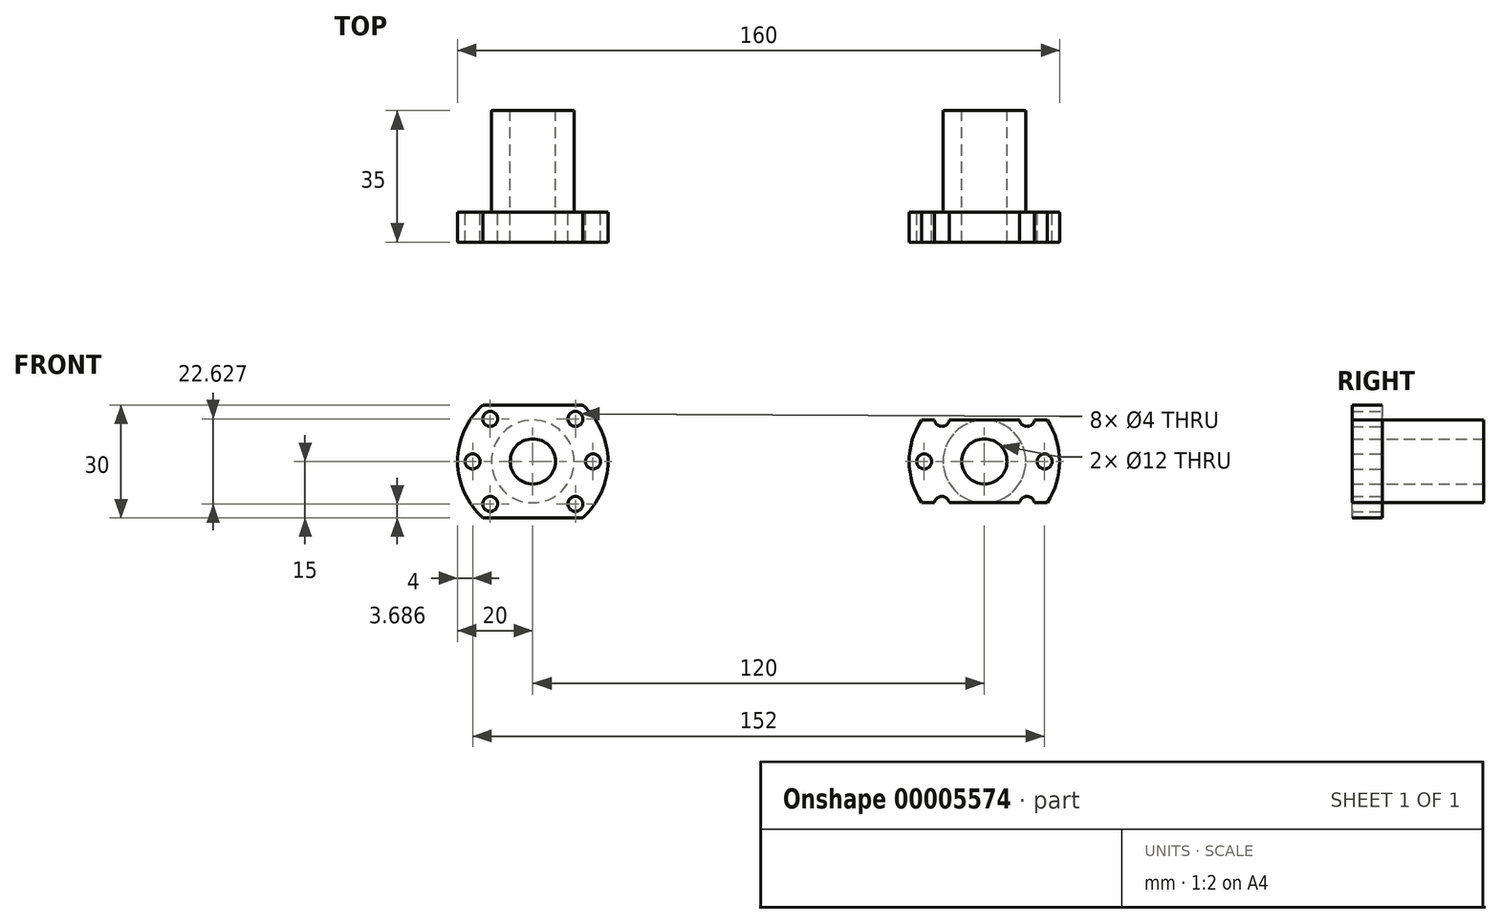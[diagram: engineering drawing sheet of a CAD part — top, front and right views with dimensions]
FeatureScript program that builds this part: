
annotation { "Feature Type Name" : "Feature", "Feature Type Description" : "" }
export const myFeature = defineFeature(function(context is Context, id is Id, definition is map)
    precondition{}
    {
        {
            var Q0;
            Q0=qCreatedBy(makeId("Front.planeOp"),FACE);
            var sketch = newSketch(context, id + "F0", { "sketchPlane" : qUnion([Q0])});
            skArc(sketch, "E0", {"start": v(-13.23, 15) * mm, "mid": v(-20, 0) * mm, "end": v(-13.23, -15) * mm});
            skLineSegment(sketch, "E1", {"start": v(-23.41, 15) * mm, "end": v(25.17, 15) * mm, "construction": true});
            skLineSegment(sketch, "E2", {"start": v(-13.23, 15) * mm, "end": v(13.23, 15) * mm});
            skLineSegment(sketch, "E3.0.MirrorCS", {"start": v(-13.23, -15) * mm, "end": v(13.23, -15) * mm});
            skArc(sketch, "E4.trimOffspring", {"start": v(13.23, -15) * mm, "mid": v(20, 0) * mm, "end": v(13.23, 15) * mm});
            skCircle(sketch, "E5", {"center": v(0, 0) * mm, "radius": 16 * mm, "construction": true});
            skCircle(sketch, "E6", {"center": v(-16, 0) * mm, "radius": 2 * mm});
            skCircle(sketch, "E7.1.0", {"center": v(-11.31, 11.31) * mm, "radius": 2 * mm});
            skLineSegment(sketch, "E7.anchor1", {"start": v(0, 0) * mm, "end": v(-16, 0) * mm, "construction": true});
            skLineSegment(sketch, "E7.anchor2", {"start": v(0, 0) * mm, "end": v(-11.31, 11.31) * mm, "construction": true});
            skCircle(sketch, "E8.0.MirrorC", {"center": v(-11.31, -11.31) * mm, "radius": 2 * mm});
            skCircle(sketch, "E9.0.MirrorC", {"center": v(11.31, 11.31) * mm, "radius": 2 * mm});
            skCircle(sketch, "E10.0.MirrorC", {"center": v(16, 0) * mm, "radius": 2 * mm});
            skCircle(sketch, "E11.0.MirrorC", {"center": v(11.31, -11.31) * mm, "radius": 2 * mm});
            skCircle(sketch, "E12", {"center": v(0, 0) * mm, "radius": 6 * mm});
            skLineSegment(sketch, "E13", {"start": v(-18.41, 10.23) * mm, "end": v(26.14, 10.23) * mm, "construction": true});
            skSolve(sketch);
        }
        {
            var Q0;
            Q0=makeQuery(id+"F0.imprint","IMPRINT",FACE,{"disambiguationData":[TD([[makeQuery(id+"F0.imprint","IMPRINT",EDGE,{"derivedFrom":sQuery(id+"F0.wireOp",EDGE,"E0")}),1.0]])]});
            extrude(context, id + "F1", {"entities" : qUnion([Q0]), "depth" : 8 * mm});
        }
        {
            var Q0;
            Q0=makeQuery(id+"F1.opExtrude","CAP_FACE",FACE,{"disambiguationData":[OSD([sQuery(id+"F0.wireOp",EDGE,"E0"),sQuery(id+"F0.wireOp",EDGE,"E2"),sQuery(id+"F0.wireOp",EDGE,"E3.0.MirrorCS"),sQuery(id+"F0.wireOp",EDGE,"E4.trimOffspring"),sQuery(id+"F0.wireOp",EDGE,"E6"),sQuery(id+"F0.wireOp",EDGE,"E7.1.0"),sQuery(id+"F0.wireOp",EDGE,"E8.0.MirrorC"),sQuery(id+"F0.wireOp",EDGE,"E9.0.MirrorC"),sQuery(id+"F0.wireOp",EDGE,"E10.0.MirrorC"),sQuery(id+"F0.wireOp",EDGE,"E11.0.MirrorC"),sQuery(id+"F0.wireOp",EDGE,"E12")])],"isStart":true});
            var sketch = newSketch(context, id + "F2", { "sketchPlane" : qUnion([Q0])});
            skCircle(sketch, "E14", {"center": v(0, 0) * mm, "radius": 11 * mm});
            skCircle(sketch, "E15", {"center": v(0, 0) * mm, "radius": 6 * mm});
            skSolve(sketch);
        }
        {
            var Q0;
            Q0=makeQuery(id+"F2.imprint","IMPRINT",FACE,{"disambiguationData":[TD([[makeQuery(id+"F2.imprint","IMPRINT",EDGE,{"derivedFrom":sQuery(id+"F2.wireOp",EDGE,"E14")}),1.0]])]});
            extrude(context, id + "F3", {"entities" : qUnion([Q0]), "operationType" : NewBodyOperationType.ADD, "depth" : 27 * mm});
        }
        {
            var Q0;
            Q0=makeQuery(id+"F1.opExtrude","SWEPT_BODY",BODY,{"disambiguationData":[OSD([sQuery(id+"F0.wireOp",EDGE,"E0"),sQuery(id+"F0.wireOp",EDGE,"E2"),sQuery(id+"F0.wireOp",EDGE,"E3.0.MirrorCS"),sQuery(id+"F0.wireOp",EDGE,"E4.trimOffspring"),sQuery(id+"F0.wireOp",EDGE,"E6"),sQuery(id+"F0.wireOp",EDGE,"E7.1.0"),sQuery(id+"F0.wireOp",EDGE,"E8.0.MirrorC"),sQuery(id+"F0.wireOp",EDGE,"E9.0.MirrorC"),sQuery(id+"F0.wireOp",EDGE,"E10.0.MirrorC"),sQuery(id+"F0.wireOp",EDGE,"E11.0.MirrorC"),sQuery(id+"F0.wireOp",EDGE,"E12")])]});
            transform(context, id + "F4", {"entities" : qUnion([Q0]), "transformType" : TransformType.TRANSLATION_3D, "dx" : 120 * mm, "dy" : 0 * mm, "dz" : 0 * mm, "makeCopy" : true});
        }
        {
            var Q0;
            Q0=makeQuery(id+"F4.opPattern","COPY",FACE,{"derivedFrom":makeQuery(id+"F1.opExtrude","CAP_FACE",FACE,{"disambiguationData":[OSD([sQuery(id+"F0.wireOp",EDGE,"E0"),sQuery(id+"F0.wireOp",EDGE,"E2"),sQuery(id+"F0.wireOp",EDGE,"E3.0.MirrorCS"),sQuery(id+"F0.wireOp",EDGE,"E4.trimOffspring"),sQuery(id+"F0.wireOp",EDGE,"E6"),sQuery(id+"F0.wireOp",EDGE,"E7.1.0"),sQuery(id+"F0.wireOp",EDGE,"E8.0.MirrorC"),sQuery(id+"F0.wireOp",EDGE,"E9.0.MirrorC"),sQuery(id+"F0.wireOp",EDGE,"E10.0.MirrorC"),sQuery(id+"F0.wireOp",EDGE,"E11.0.MirrorC"),sQuery(id+"F0.wireOp",EDGE,"E12")])],"isStart":false}),"instanceName":"1"});
            var sketch = newSketch(context, id + "F5", { "sketchPlane" : qUnion([Q0])});
            skLineSegment(sketch, "E16", {"start": v(-4.25, 11) * mm, "end": v(109.82, 11) * mm, "construction": true});
            skLineSegment(sketch, "E17.bottom", {"start": v(103.3, 11) * mm, "end": v(136.7, 11) * mm});
            skLineSegment(sketch, "E17.top", {"start": v(103.3, 15) * mm, "end": v(136.7, 15) * mm});
            skLineSegment(sketch, "E17.left", {"start": v(103.3, 11) * mm, "end": v(103.3, 15) * mm});
            skLineSegment(sketch, "E17.right", {"start": v(136.7, 11) * mm, "end": v(136.7, 15) * mm});
            skLineSegment(sketch, "E18", {"start": v(136, 0) * mm, "end": v(104, 0) * mm, "construction": true});
            skLineSegment(sketch, "E19.0.MirrorCS", {"start": v(103.3, -11) * mm, "end": v(103.3, -15) * mm});
            skLineSegment(sketch, "E19.1.MirrorCS", {"start": v(103.3, -15) * mm, "end": v(136.7, -15) * mm});
            skLineSegment(sketch, "E19.2.MirrorCS", {"start": v(103.3, -11) * mm, "end": v(136.7, -11) * mm});
            skLineSegment(sketch, "E19.3.MirrorCS", {"start": v(136.7, -11) * mm, "end": v(136.7, -15) * mm});
            skLineSegment(sketch, "E20", {"start": v(100, 11) * mm, "end": v(100, -15) * mm, "construction": true});
            skLineSegment(sketch, "E21", {"start": v(100, 11) * mm, "end": v(100, -9.43) * mm, "construction": true});
            skLineSegment(sketch, "E22", {"start": v(120, 0) * mm, "end": v(120, 11) * mm, "construction": true});
            skLineSegment(sketch, "E23.bottom", {"start": v(100, 11) * mm, "end": v(100, 11) * mm});
            skLineSegment(sketch, "E23.top", {"start": v(100, -9.43) * mm, "end": v(100, -9.43) * mm});
            skLineSegment(sketch, "E23.left", {"start": v(100, 11) * mm, "end": v(100, -9.43) * mm});
            skLineSegment(sketch, "E23.right", {"start": v(100, 11) * mm, "end": v(100, -9.43) * mm});
            skLineSegment(sketch, "E24.0.MirrorCS", {"start": v(140, -9.43) * mm, "end": v(140, -9.43) * mm});
            skLineSegment(sketch, "E24.1.MirrorCS", {"start": v(140, 11) * mm, "end": v(140, -9.43) * mm, "construction": true});
            skLineSegment(sketch, "E24.2.MirrorCS", {"start": v(140, 11) * mm, "end": v(140, -9.43) * mm});
            skLineSegment(sketch, "E24.3.MirrorCS", {"start": v(140, 11) * mm, "end": v(140, -9.43) * mm});
            skLineSegment(sketch, "E24.4.MirrorCS", {"start": v(140, 11) * mm, "end": v(140, 11) * mm});
            skLineSegment(sketch, "E25", {"start": v(103.14, -2.9) * mm, "end": v(56.83, -2.9) * mm, "construction": true});
            skLineSegment(sketch, "E26", {"start": v(102, 3.87) * mm, "end": v(102, -2.9) * mm, "construction": true});
            skLineSegment(sketch, "E27", {"start": v(138, 3.4) * mm, "end": v(138, -2.9) * mm, "construction": true});
            skSolve(sketch);
        }
        {
            var Q0;
            {var subQ0=makeQuery(id+"F4.opPattern","COPY",EDGE,{"derivedFrom":makeQuery(id+"F1.opExtrude","CAP_EDGE",EDGE,{"disambiguationData":[OSD([sQuery(id+"F0.wireOp",EDGE,"E0")])],"isStart":false}),"instanceName":"1"});var subQ1=sQuery(id+"F5.wireOp",EDGE,"E17.bottom");var subQ2=makeQuery(id+"F5.imprint","INTERSECT",VERTEX,{"derivedFrom":[subQ0,subQ1]});var subQ6=sQuery(id+"F5.wireOp",EDGE,"E17.left");var subQ11=sQuery(id+"F5.wireOp",EDGE,"E17.right");var subQ12=sQuery(id+"F5.wireOp",EDGE,"E19.2.MirrorCS");var subQ14=sQuery(id+"F5.wireOp",EDGE,"E19.1.MirrorCS");var subQ15=makeQuery(id+"F5.imprint","INTERSECT",VERTEX,{"derivedFrom":[subQ0,subQ14]});var subQ17=sQuery(id+"F5.wireOp",EDGE,"E19.0.MirrorCS");var subQ21=sQuery(id+"F5.wireOp",EDGE,"E19.3.MirrorCS");var subQ22=makeQuery(id+"F4.opPattern","COPY",EDGE,{"derivedFrom":makeQuery(id+"F1.opExtrude","CAP_EDGE",EDGE,{"disambiguationData":[OSD([sQuery(id+"F0.wireOp",EDGE,"E9.0.MirrorC")])],"isStart":false}),"instanceName":"1"});var subQ24=makeQuery(id+"F5.imprint","INTERSECT",VERTEX,{"disambiguationData":[OD(0.0)],"derivedFrom":[subQ22,subQ1]});var subQ26=makeQuery(id+"F4.opPattern","COPY",EDGE,{"derivedFrom":makeQuery(id+"F1.opExtrude","CAP_EDGE",EDGE,{"disambiguationData":[OSD([sQuery(id+"F0.wireOp",EDGE,"E7.1.0")])],"isStart":false}),"instanceName":"1"});var subQ28=makeQuery(id+"F5.imprint","INTERSECT",VERTEX,{"disambiguationData":[OD(0.0)],"derivedFrom":[subQ26,subQ1]});var subQ30=makeQuery(id+"F4.opPattern","COPY",EDGE,{"derivedFrom":makeQuery(id+"F1.opExtrude","CAP_EDGE",EDGE,{"disambiguationData":[OSD([sQuery(id+"F0.wireOp",EDGE,"E11.0.MirrorC")])],"isStart":false}),"instanceName":"1"});var subQ32=makeQuery(id+"F5.imprint","INTERSECT",VERTEX,{"disambiguationData":[OD(0.0)],"derivedFrom":[subQ30,subQ12]});var subQ34=makeQuery(id+"F4.opPattern","COPY",EDGE,{"derivedFrom":makeQuery(id+"F1.opExtrude","CAP_EDGE",EDGE,{"disambiguationData":[OSD([sQuery(id+"F0.wireOp",EDGE,"E8.0.MirrorC")])],"isStart":false}),"instanceName":"1"});var subQ36=makeQuery(id+"F5.imprint","INTERSECT",VERTEX,{"disambiguationData":[OD(0.0)],"derivedFrom":[subQ34,subQ12]});Q0=qUnion([makeQuery(id+"F5.imprint","IMPRINT",FACE,{"disambiguationData":[TD([[makeQuery(id+"F5.imprint","IMPRINT",EDGE,{"derivedFrom":subQ6}),-1.0]])]}),makeQuery(id+"F5.imprint","IMPRINT",FACE,{"disambiguationData":[TD([[makeQuery(id+"F5.imprint","IMPRINT",EDGE,{"derivedFrom":subQ11}),1.0]])]}),makeQuery(id+"F5.imprint","IMPRINT",FACE,{"disambiguationData":[TD([[makeQuery(id+"F5.imprint","IMPRINT",EDGE,{"derivedFrom":subQ17}),1.0]])]}),makeQuery(id+"F5.imprint","IMPRINT",FACE,{"disambiguationData":[TD([[makeQuery(id+"F5.imprint","IMPRINT",EDGE,{"derivedFrom":subQ21}),-1.0]])]}),makeQuery(id+"F5.imprint","IMPRINT",FACE,{"disambiguationData":[TD([[makeQuery(id+"F5.imprint","IMPRINT",EDGE,{"disambiguationData":[TD([[subQ2,-1.0]])],"derivedFrom":subQ1}),1.0]])]}),makeQuery(id+"F5.imprint","IMPRINT",FACE,{"disambiguationData":[TD([[makeQuery(id+"F5.imprint","IMPRINT",EDGE,{"disambiguationData":[TD([[subQ15,-1.0]])],"derivedFrom":subQ14}),1.0]])]}),makeQuery(id+"F5.imprint","IMPRINT",FACE,{"disambiguationData":[TD([[makeQuery(id+"F5.imprint","IMPRINT",EDGE,{"disambiguationData":[TD([[subQ28,-1.0]])],"derivedFrom":subQ1}),1.0]])]}),makeQuery(id+"F5.imprint","IMPRINT",FACE,{"disambiguationData":[TD([[makeQuery(id+"F5.imprint","IMPRINT",EDGE,{"disambiguationData":[TD([[subQ24,-1.0]])],"derivedFrom":subQ1}),1.0]])]}),makeQuery(id+"F5.imprint","IMPRINT",FACE,{"disambiguationData":[TD([[makeQuery(id+"F5.imprint","IMPRINT",EDGE,{"disambiguationData":[TD([[subQ36,-1.0]])],"derivedFrom":subQ12}),-1.0]])]}),makeQuery(id+"F5.imprint","IMPRINT",FACE,{"disambiguationData":[TD([[makeQuery(id+"F5.imprint","IMPRINT",EDGE,{"disambiguationData":[TD([[subQ32,-1.0]])],"derivedFrom":subQ12}),-1.0]])]})]);}
            var Q1;
            {var subQ0=makeQuery(id+"F4.opPattern","COPY",EDGE,{"derivedFrom":makeQuery(id+"F1.opExtrude","CAP_EDGE",EDGE,{"disambiguationData":[OSD([sQuery(id+"F0.wireOp",EDGE,"E0")])],"isStart":false}),"instanceName":"1"});var subQ2=sQuery(id+"F5.wireOp",EDGE,"E23.left");var subQ4=makeQuery(id+"F5.imprint","INTERSECT",VERTEX,{"disambiguationData":[OD(0.0)],"derivedFrom":[subQ0,subQ2]});Q1=makeQuery(id+"F5.imprint","IMPRINT",FACE,{"disambiguationData":[TD([[makeQuery(id+"F5.imprint","IMPRINT",EDGE,{"disambiguationData":[TD([[subQ4,-1.0]])],"derivedFrom":subQ2}),-1.0]])]});}
            var Q2;
            {var subQ0=makeQuery(id+"F4.opPattern","COPY",EDGE,{"derivedFrom":makeQuery(id+"F1.opExtrude","CAP_EDGE",EDGE,{"disambiguationData":[OSD([sQuery(id+"F0.wireOp",EDGE,"E4.trimOffspring")])],"isStart":false}),"instanceName":"1"});var subQ1=sQuery(id+"F5.wireOp",EDGE,"E24.3.MirrorCS");var subQ4=makeQuery(id+"F5.imprint","INTERSECT",VERTEX,{"disambiguationData":[OD(0.0)],"derivedFrom":[subQ0,subQ1]});Q2=makeQuery(id+"F5.imprint","IMPRINT",FACE,{"disambiguationData":[TD([[makeQuery(id+"F5.imprint","IMPRINT",EDGE,{"disambiguationData":[TD([[subQ4,-1.0]])],"derivedFrom":subQ1}),1.0]])]});}
            var Q3;
            Q3=makeQuery(id+"F4.opPattern","COPY",FACE,{"derivedFrom":makeQuery(id+"F1.opExtrude","CAP_FACE",FACE,{"disambiguationData":[OSD([sQuery(id+"F0.wireOp",EDGE,"E0"),sQuery(id+"F0.wireOp",EDGE,"E2"),sQuery(id+"F0.wireOp",EDGE,"E3.0.MirrorCS"),sQuery(id+"F0.wireOp",EDGE,"E4.trimOffspring"),sQuery(id+"F0.wireOp",EDGE,"E6"),sQuery(id+"F0.wireOp",EDGE,"E7.1.0"),sQuery(id+"F0.wireOp",EDGE,"E8.0.MirrorC"),sQuery(id+"F0.wireOp",EDGE,"E9.0.MirrorC"),sQuery(id+"F0.wireOp",EDGE,"E10.0.MirrorC"),sQuery(id+"F0.wireOp",EDGE,"E11.0.MirrorC"),sQuery(id+"F0.wireOp",EDGE,"E12")])],"isStart":true}),"instanceName":"1"});
            extrude(context, id + "F6", {"entities" : qUnion([Q0, Q1, Q2]), "operationType" : NewBodyOperationType.REMOVE, "endBound" : BoundingType.UP_TO_SURFACE, "oppositeDirection" : true, "endBoundEntityFace" : qUnion([Q3]), "depth" : 25 * mm});
        }
    });
